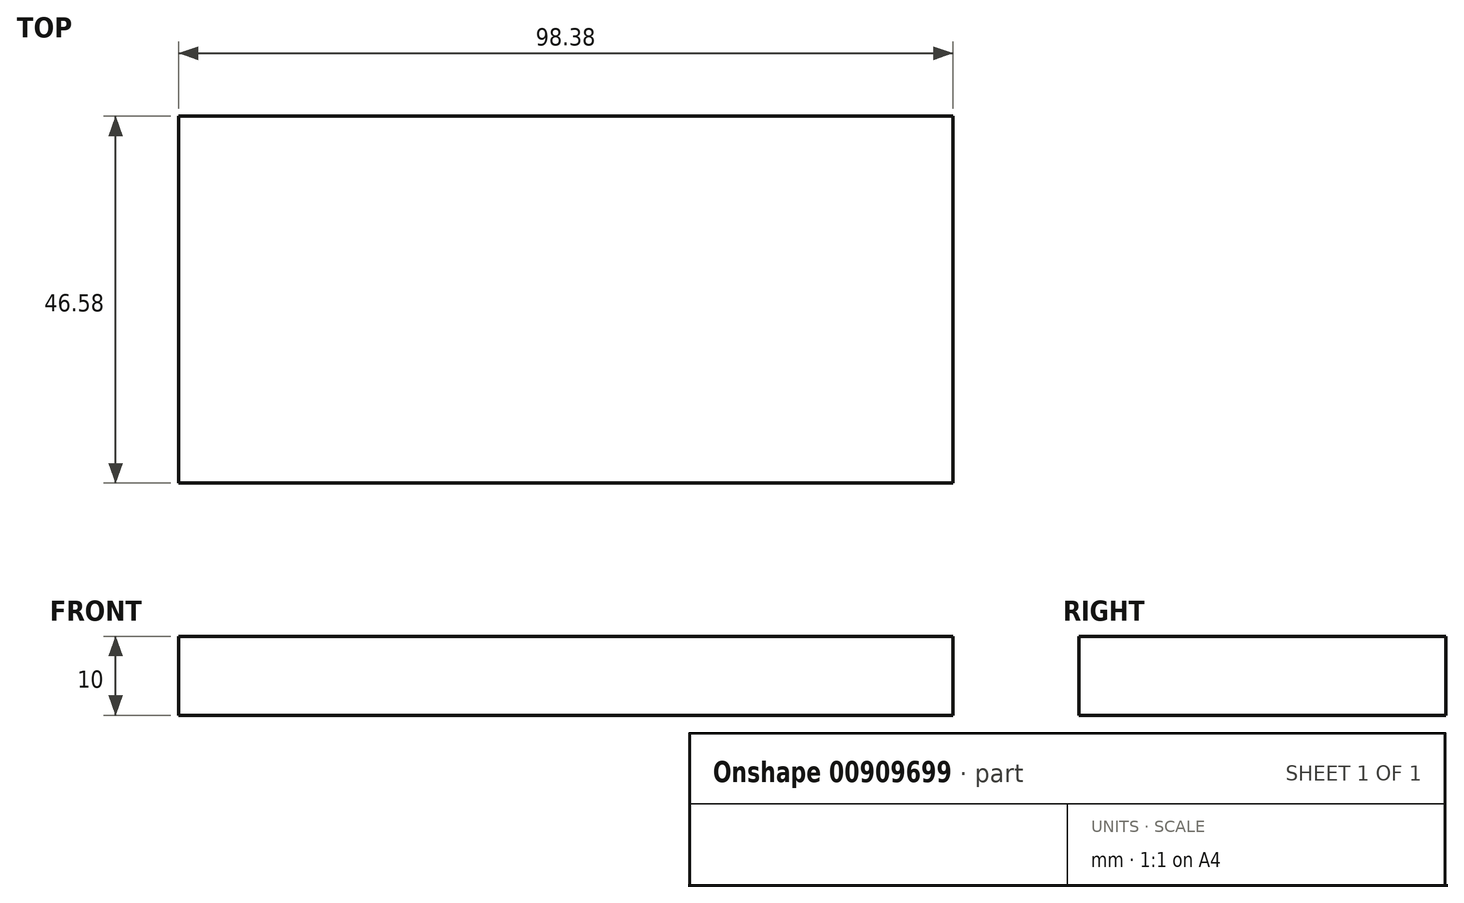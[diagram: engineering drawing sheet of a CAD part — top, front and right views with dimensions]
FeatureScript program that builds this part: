
annotation { "Feature Type Name" : "Feature", "Feature Type Description" : "" }
export const myFeature = defineFeature(function(context is Context, id is Id, definition is map)
    precondition{}
    {
        {
            var Q0;
            Q0=qCreatedBy(makeId("Top.planeOp"),FACE);
            var sketch = newSketch(context, id + "F0", { "sketchPlane" : qUnion([Q0])});
            skLineSegment(sketch, "E0.bottom", {"start": v(49.19, 23.3) * mm, "end": v(-49.19, 23.3) * mm});
            skLineSegment(sketch, "E0.top", {"start": v(49.19, -23.3) * mm, "end": v(-49.19, -23.3) * mm});
            skLineSegment(sketch, "E0.left", {"start": v(49.19, 23.3) * mm, "end": v(49.19, -23.3) * mm});
            skLineSegment(sketch, "E0.right", {"start": v(-49.19, 23.3) * mm, "end": v(-49.19, -23.3) * mm});
            skPoint(sketch, "E0.middle", {"position": v(0, 0) * mm});
            skSolve(sketch);
        }
        {
            var Q0;
            Q0 = qSketchRegion(id + "F0", true);
            extrude(context, id + "F1", {"entities" : qUnion([Q0]), "depth" : 10 * mm, "offsetDistance" : 25 * mm});
        }
    });
